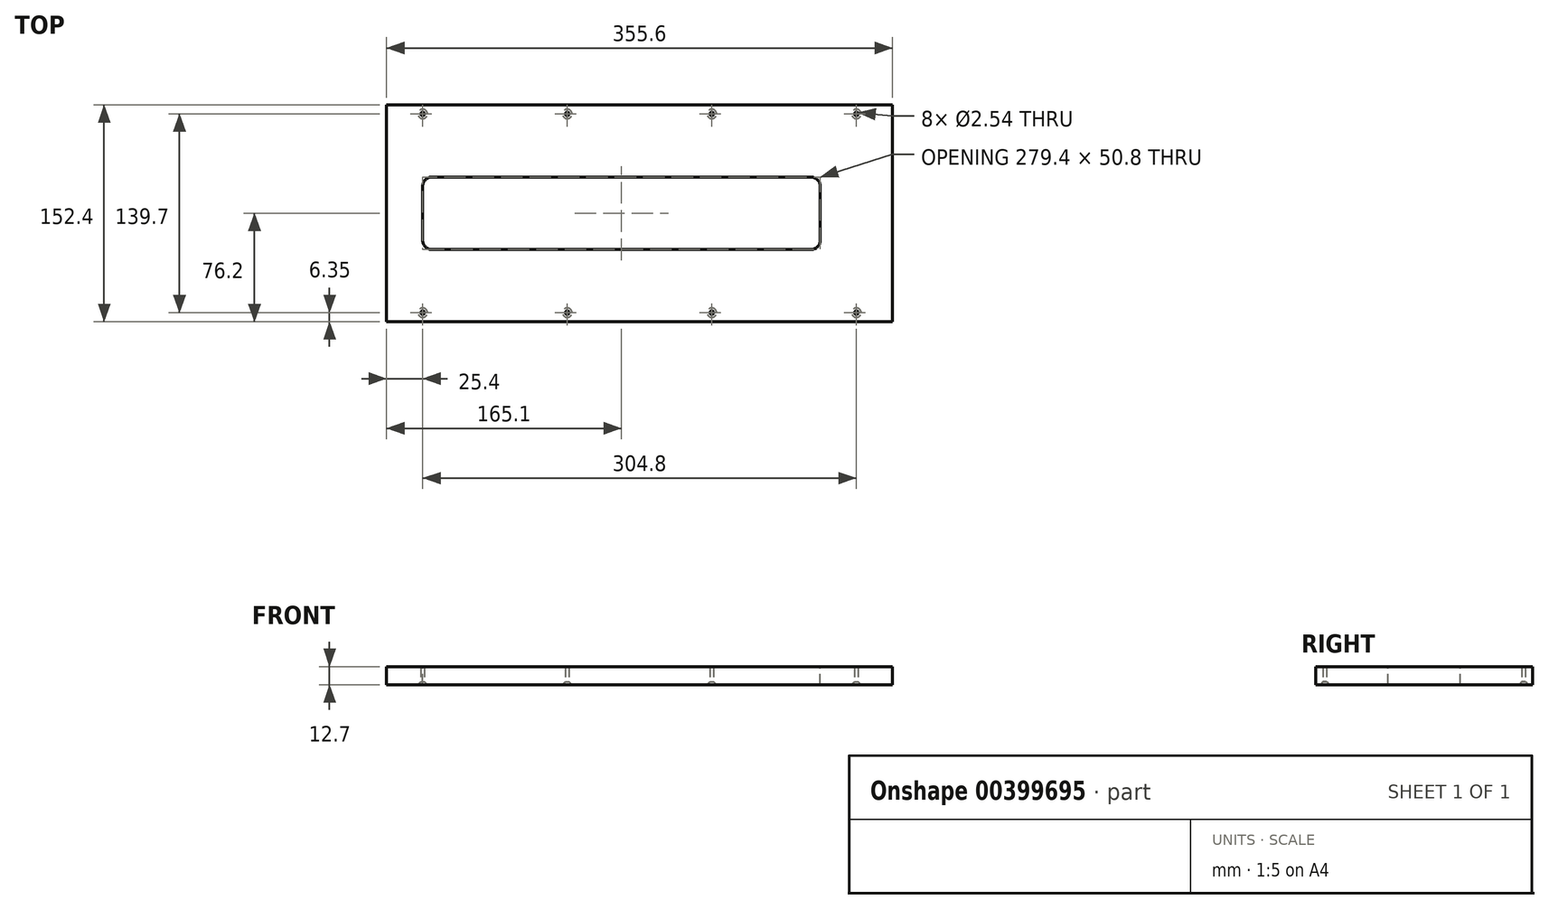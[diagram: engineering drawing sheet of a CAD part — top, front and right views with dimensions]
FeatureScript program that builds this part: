
annotation { "Feature Type Name" : "Feature", "Feature Type Description" : "" }
export const myFeature = defineFeature(function(context is Context, id is Id, definition is map)
    precondition{}
    {
        {
            var Q0;
            Q0=qCreatedBy(makeId("Top.planeOp"),FACE);
            var sketch = newSketch(context, id + "F0", { "sketchPlane" : qUnion([Q0])});
            skLineSegment(sketch, "E0.bottom", {"start": v(-177.8, 76.2) * mm, "end": v(177.8, 76.2) * mm});
            skLineSegment(sketch, "E0.top", {"start": v(-177.8, -76.2) * mm, "end": v(177.8, -76.2) * mm});
            skLineSegment(sketch, "E0.left", {"start": v(-177.8, 76.2) * mm, "end": v(-177.8, -76.2) * mm});
            skLineSegment(sketch, "E0.right", {"start": v(177.8, 76.2) * mm, "end": v(177.8, -76.2) * mm});
            skSolve(sketch);
        }
        {
            var Q0;
            Q0=makeQuery(id+"F0.imprint","IMPRINT",FACE,{"disambiguationData":[TD([[makeQuery(id+"F0.imprint","IMPRINT",EDGE,{"derivedFrom":sQuery(id+"F0.wireOp",EDGE,"E0.bottom")}),-1.0]])]});
            extrude(context, id + "F1", {"entities" : qUnion([Q0]), "depth" : 12.7 * mm});
        }
        {
            var Q0;
            Q0=makeQuery(id+"F1.opExtrude","CAP_FACE",FACE,{"disambiguationData":[OSD([sQuery(id+"F0.wireOp",EDGE,"E0.bottom"),sQuery(id+"F0.wireOp",EDGE,"E0.top"),sQuery(id+"F0.wireOp",EDGE,"E0.left"),sQuery(id+"F0.wireOp",EDGE,"E0.right")])],"isStart":false});
            var sketch = newSketch(context, id + "F2", { "sketchPlane" : qUnion([Q0])});
            skLineSegment(sketch, "E1.bottom", {"start": v(-146.05, 25.4) * mm, "end": v(120.65, 25.4) * mm});
            skLineSegment(sketch, "E1.top", {"start": v(-146.05, -25.4) * mm, "end": v(120.65, -25.4) * mm});
            skLineSegment(sketch, "E1.left", {"start": v(-152.4, 19.05) * mm, "end": v(-152.4, -19.05) * mm});
            skLineSegment(sketch, "E1.right", {"start": v(127, 19.05) * mm, "end": v(127, -19.05) * mm});
            skLineSegment(sketch, "E2.0", {"start": v(-177.8, 76.2) * mm, "end": v(-177.8, -76.2) * mm, "construction": true});
            skLineSegment(sketch, "E3.0", {"start": v(177.8, 76.2) * mm, "end": v(177.8, -76.2) * mm, "construction": true});
            skPoint(sketch, "E4.visualSharp", {"position": v(-152.4, -25.4) * mm});
            skArc(sketch, "E4.filletArc", {"start": v(-152.4, -19.05) * mm, "mid": v(-150.54, -23.54) * mm, "end": v(-146.05, -25.4) * mm});
            skPoint(sketch, "E5.visualSharp", {"position": v(-152.4, 25.4) * mm});
            skArc(sketch, "E5.filletArc", {"start": v(-146.05, 25.4) * mm, "mid": v(-150.54, 23.54) * mm, "end": v(-152.4, 19.05) * mm});
            skPoint(sketch, "E6.visualSharp", {"position": v(127, 25.4) * mm});
            skArc(sketch, "E6.filletArc", {"start": v(127, 19.05) * mm, "mid": v(125.14, 23.54) * mm, "end": v(120.65, 25.4) * mm});
            skPoint(sketch, "E7.visualSharp", {"position": v(127, -25.4) * mm});
            skArc(sketch, "E7.filletArc", {"start": v(120.65, -25.4) * mm, "mid": v(125.14, -23.54) * mm, "end": v(127, -19.05) * mm});
            skSolve(sketch);
        }
        {
            var Q0;
            Q0=makeQuery(id+"F2.imprint","IMPRINT",FACE,{"disambiguationData":[TD([[makeQuery(id+"F2.imprint","IMPRINT",EDGE,{"derivedFrom":sQuery(id+"F2.wireOp",EDGE,"E1.bottom")}),-1.0]])]});
            extrude(context, id + "F3", {"entities" : qUnion([Q0]), "operationType" : NewBodyOperationType.REMOVE, "endBound" : BoundingType.THROUGH_ALL, "oppositeDirection" : true, "depth" : 25.4 * mm});
        }
        {
            var Q0;
            Q0=makeQuery(id+"F1.opExtrude","CAP_FACE",FACE,{"disambiguationData":[OSD([sQuery(id+"F0.wireOp",EDGE,"E0.bottom"),sQuery(id+"F0.wireOp",EDGE,"E0.top"),sQuery(id+"F0.wireOp",EDGE,"E0.left"),sQuery(id+"F0.wireOp",EDGE,"E0.right")])],"isStart":true});
            var sketch = newSketch(context, id + "F4", { "sketchPlane" : qUnion([Q0])});
            skLineSegment(sketch, "E8", {"start": v(-177.8, 69.85) * mm, "end": v(177.8, 69.85) * mm, "construction": true});
            skPoint(sketch, "E9", {"position": v(-152.4, 69.85) * mm});
            skPoint(sketch, "E10", {"position": v(152.4, 69.85) * mm});
            skPoint(sketch, "E11", {"position": v(-50.8, 69.85) * mm});
            skPoint(sketch, "E12", {"position": v(50.8, 69.85) * mm});
            skLineSegment(sketch, "E13", {"start": v(-177.8, 0) * mm, "end": v(177.8, 0) * mm, "construction": true});
            skPoint(sketch, "E14.MirrorP", {"position": v(-152.4, -69.85) * mm});
            skPoint(sketch, "E15.MirrorP", {"position": v(-50.8, -69.85) * mm});
            skPoint(sketch, "E16.MirrorP", {"position": v(50.8, -69.85) * mm});
            skPoint(sketch, "E17.MirrorP", {"position": v(152.4, -69.85) * mm});
            skSolve(sketch);
        }
        {
            var Q0;
            Q0=sQuery(id+"F4.wireOp",VERTEX,"E9");
            var Q1;
            Q1=sQuery(id+"F4.wireOp",VERTEX,"E11");
            var Q2;
            Q2=sQuery(id+"F4.wireOp",VERTEX,"E12");
            var Q3;
            Q3=sQuery(id+"F4.wireOp",VERTEX,"E10");
            var Q4;
            Q4=sQuery(id+"F4.wireOp",VERTEX,"E17.MirrorP");
            var Q5;
            Q5=sQuery(id+"F4.wireOp",VERTEX,"E16.MirrorP");
            var Q6;
            Q6=sQuery(id+"F4.wireOp",VERTEX,"E15.MirrorP");
            var Q7;
            Q7=sQuery(id+"F4.wireOp",VERTEX,"E14.MirrorP");
            var Q8;
            Q8=makeQuery(id+"F1.opExtrude","SWEPT_BODY",BODY,{"disambiguationData":[OSD([sQuery(id+"F0.wireOp",EDGE,"E0.bottom"),sQuery(id+"F0.wireOp",EDGE,"E0.top"),sQuery(id+"F0.wireOp",EDGE,"E0.left"),sQuery(id+"F0.wireOp",EDGE,"E0.right")])]});
            hole(context, id + "F5", {"style" : HoleStyle.C_SINK, "endStyle" : HoleEndStyle.THROUGH, "holeDiameter" : 2.54 * mm, "cSinkDiameter" : 6.6 * mm, "cSinkAngle" : 90 * degree, "isTappedThrough" : true, "tappedDepth" : 12.7 * mm, "tapClearance" : 3, "locations" : qUnion([Q0, Q1, Q2, Q3, Q4, Q5, Q6, Q7]), "scope" : qUnion([Q8])});
        }
    });
